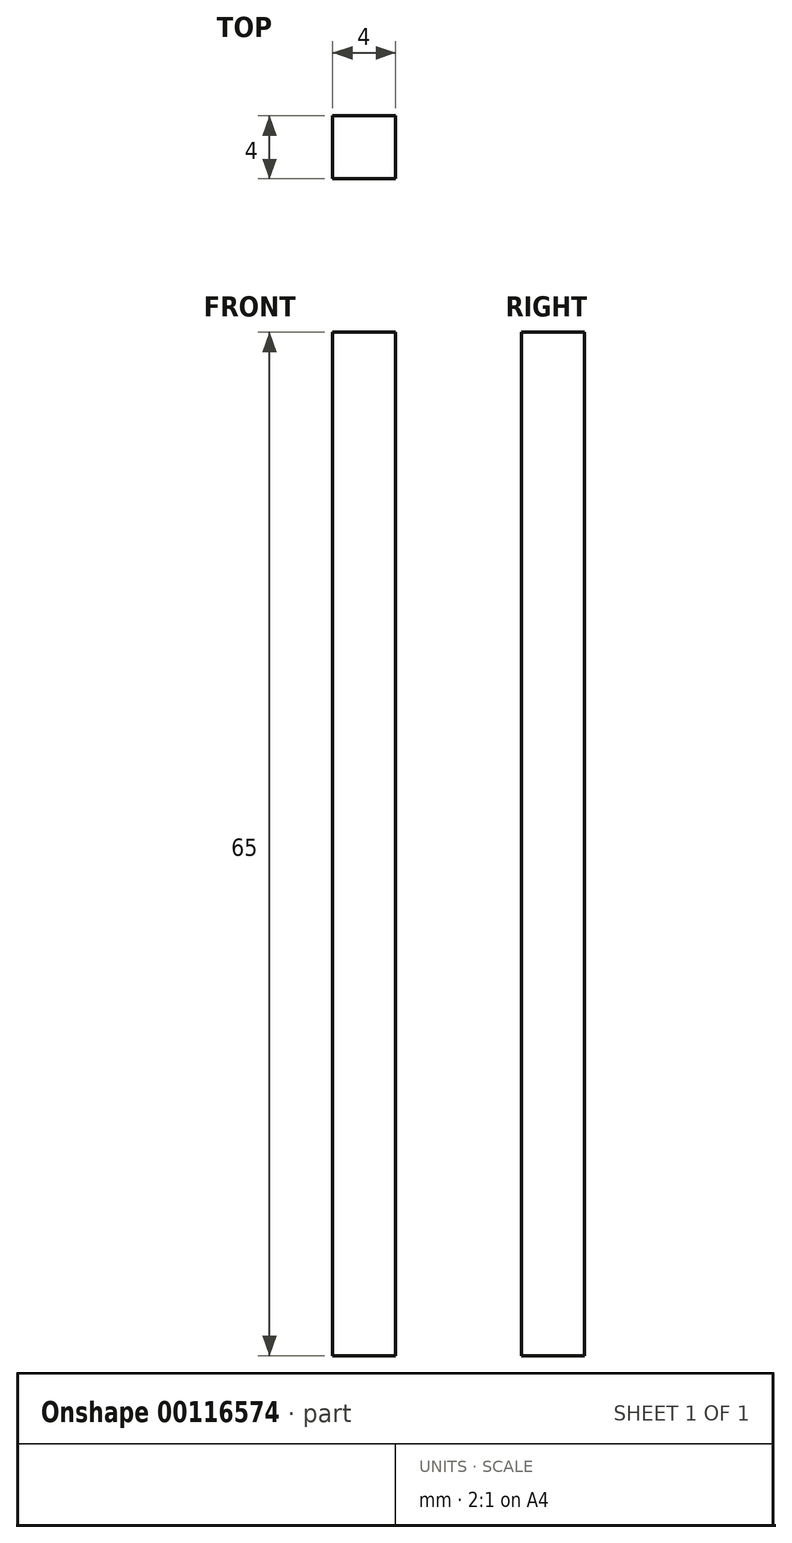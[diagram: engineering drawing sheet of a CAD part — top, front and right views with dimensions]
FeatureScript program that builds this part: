
annotation { "Feature Type Name" : "Feature", "Feature Type Description" : "" }
export const myFeature = defineFeature(function(context is Context, id is Id, definition is map)
    precondition{}
    {
        {
            var Q0;
            Q0=qCreatedBy(makeId("Top.planeOp"),FACE);
            var sketch = newSketch(context, id + "F0", { "sketchPlane" : qUnion([Q0])});
            skLineSegment(sketch, "E0.bottom", {"start": v(2, 2) * mm, "end": v(-2, 2) * mm});
            skLineSegment(sketch, "E0.top", {"start": v(2, -2) * mm, "end": v(-2, -2) * mm});
            skLineSegment(sketch, "E0.left", {"start": v(2, 2) * mm, "end": v(2, -2) * mm});
            skLineSegment(sketch, "E0.right", {"start": v(-2, 2) * mm, "end": v(-2, -2) * mm});
            skPoint(sketch, "E0.middle", {"position": v(0, 0) * mm});
            skSolve(sketch);
        }
        {
            var Q0;
            Q0=makeQuery(id+"F0.imprint","IMPRINT",FACE,{"disambiguationData":[TD([[makeQuery(id+"F0.imprint","IMPRINT",EDGE,{"derivedFrom":sQuery(id+"F0.wireOp",EDGE,"E0.bottom")}),1.0]])]});
            extrude(context, id + "F1", {"entities" : qUnion([Q0]), "depth" : 65 * mm});
        }
    });
